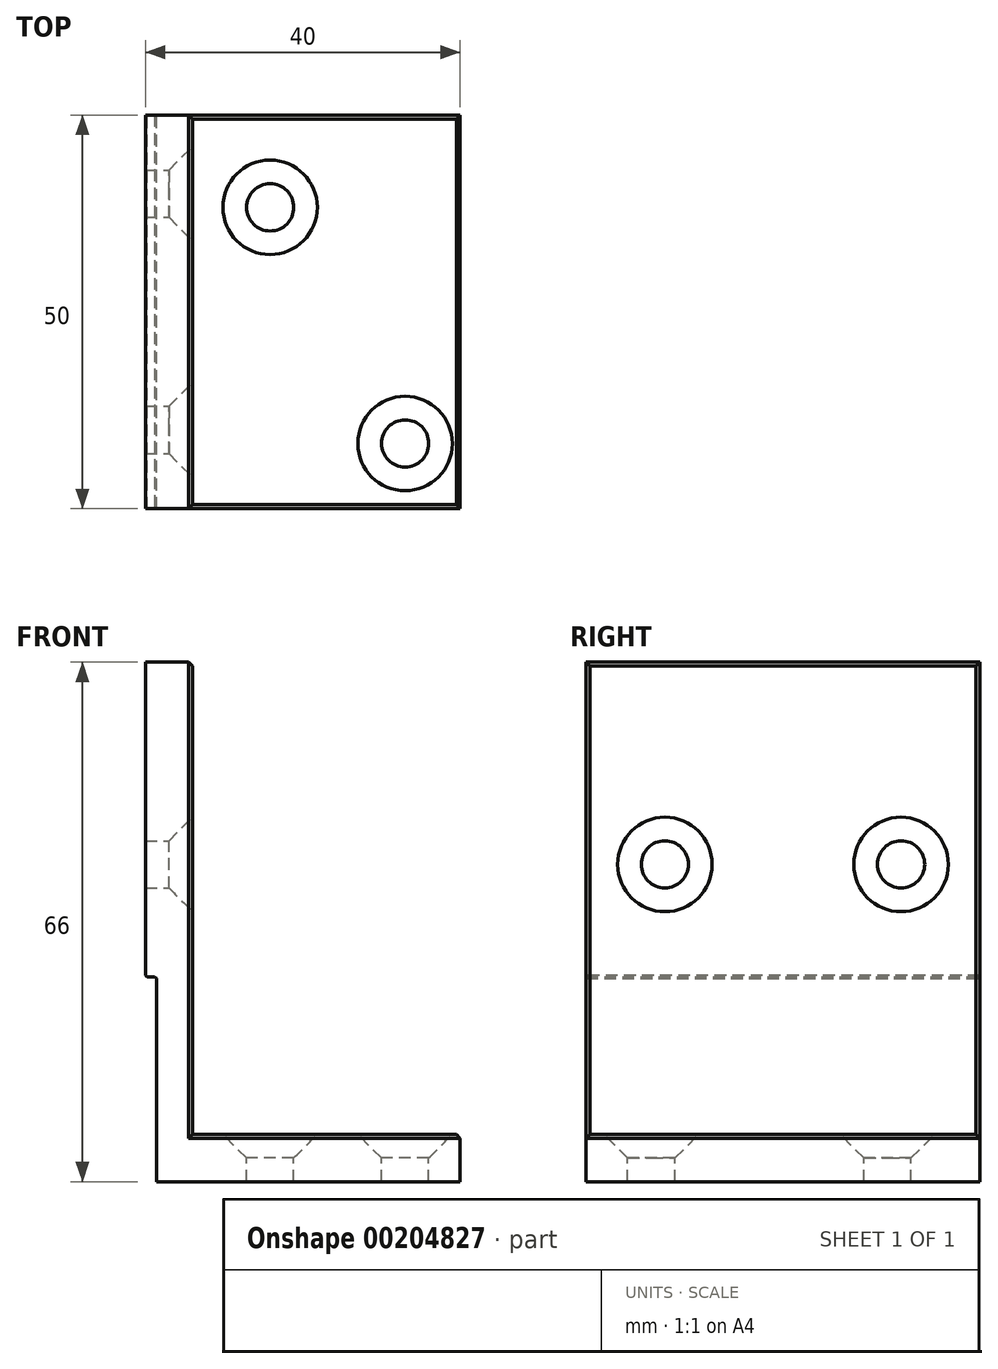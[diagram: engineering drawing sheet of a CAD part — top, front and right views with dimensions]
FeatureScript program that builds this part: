
annotation { "Feature Type Name" : "Feature", "Feature Type Description" : "" }
export const myFeature = defineFeature(function(context is Context, id is Id, definition is map)
    precondition{}
    {
        {
            var Q0;
            Q0=qCreatedBy(makeId("Front.planeOp"),FACE);
            var sketch = newSketch(context, id + "F0", { "sketchPlane" : qUnion([Q0])});
            skLineSegment(sketch, "E0", {"start": v(0, 0) * mm, "end": v(38.6, 0) * mm});
            skLineSegment(sketch, "E1", {"start": v(38.6, 0) * mm, "end": v(38.6, 6) * mm});
            skLineSegment(sketch, "E2", {"start": v(38.6, 6) * mm, "end": v(4.6, 6) * mm});
            skLineSegment(sketch, "E3", {"start": v(4.6, 6) * mm, "end": v(4.6, 66) * mm});
            skLineSegment(sketch, "E4", {"start": v(4.6, 66) * mm, "end": v(-1.4, 66) * mm});
            skLineSegment(sketch, "E5", {"start": v(-1.4, 66) * mm, "end": v(-1.4, 26) * mm});
            skLineSegment(sketch, "E6", {"start": v(-1.4, 26) * mm, "end": v(0, 26) * mm});
            skLineSegment(sketch, "E7", {"start": v(0, 26) * mm, "end": v(0, 0) * mm});
            skSolve(sketch);
        }
        {
            var Q0;
            Q0=makeQuery(id+"F0.imprint","IMPRINT",FACE,{"disambiguationData":[TD([[makeQuery(id+"F0.imprint","IMPRINT",EDGE,{"derivedFrom":sQuery(id+"F0.wireOp",EDGE,"E0")}),1.0]])]});
            extrude(context, id + "F1", {"entities" : qUnion([Q0]), "depth" : 50 * mm});
        }
        {
            var Q0;
            Q0=makeQuery(id+"F1.opExtrude","SWEPT_FACE",FACE,{"disambiguationData":[OSD([sQuery(id+"F0.wireOp",EDGE,"E3")])]});
            var sketch = newSketch(context, id + "F2", { "sketchPlane" : qUnion([Q0])});
            skCircle(sketch, "E8", {"center": v(-40, 40.3) * mm, "radius": 3 * mm});
            skCircle(sketch, "E9", {"center": v(-10, 40.3) * mm, "radius": 3 * mm});
            skSolve(sketch);
        }
        {
            var Q0;
            Q0=sQuery(id+"F2.wireOp",VERTEX,"E8.center");
            var Q1;
            Q1=sQuery(id+"F2.wireOp",VERTEX,"E9.center");
            var Q2;
            Q2=makeQuery(id+"F1.opExtrude","SWEPT_BODY",BODY,{"disambiguationData":[OSD([sQuery(id+"F0.wireOp",EDGE,"E0"),sQuery(id+"F0.wireOp",EDGE,"E1"),sQuery(id+"F0.wireOp",EDGE,"E2"),sQuery(id+"F0.wireOp",EDGE,"E3"),sQuery(id+"F0.wireOp",EDGE,"E4"),sQuery(id+"F0.wireOp",EDGE,"E5"),sQuery(id+"F0.wireOp",EDGE,"E6"),sQuery(id+"F0.wireOp",EDGE,"E7")])]});
            hole(context, id + "F3", {"style" : HoleStyle.C_SINK, "endStyle" : HoleEndStyle.BLIND, "holeDiameter" : 6 * mm, "cSinkDiameter" : 12 * mm, "cSinkAngle" : 90 * degree, "holeDepth" : 12 * mm, "startFromSketch" : true, "locations" : qUnion([Q0, Q1]), "scope" : qUnion([Q2])});
        }
        {
            var Q0;
            Q0=makeQuery(id+"F1.opExtrude","SWEPT_FACE",FACE,{"disambiguationData":[OSD([sQuery(id+"F0.wireOp",EDGE,"E2")])]});
            var sketch = newSketch(context, id + "F4", { "sketchPlane" : qUnion([Q0])});
            skCircle(sketch, "E10", {"center": v(14.45, -11.73) * mm, "radius": 3 * mm});
            skCircle(sketch, "E11", {"center": v(31.6, -41.73) * mm, "radius": 3 * mm});
            skSolve(sketch);
        }
        {
            var Q0;
            Q0=sQuery(id+"F4.wireOp",VERTEX,"E10.center");
            var Q1;
            Q1=sQuery(id+"F4.wireOp",VERTEX,"E11.center");
            var Q2;
            Q2=makeQuery(id+"F1.opExtrude","SWEPT_BODY",BODY,{"disambiguationData":[OSD([sQuery(id+"F0.wireOp",EDGE,"E0"),sQuery(id+"F0.wireOp",EDGE,"E1"),sQuery(id+"F0.wireOp",EDGE,"E2"),sQuery(id+"F0.wireOp",EDGE,"E3"),sQuery(id+"F0.wireOp",EDGE,"E4"),sQuery(id+"F0.wireOp",EDGE,"E5"),sQuery(id+"F0.wireOp",EDGE,"E6"),sQuery(id+"F0.wireOp",EDGE,"E7")])]});
            hole(context, id + "F5", {"style" : HoleStyle.C_SINK, "endStyle" : HoleEndStyle.BLIND, "holeDiameter" : 6 * mm, "cSinkDiameter" : 12 * mm, "cSinkAngle" : 90 * degree, "holeDepth" : 12 * mm, "startFromSketch" : true, "locations" : qUnion([Q0, Q1]), "scope" : qUnion([Q2])});
        }
        {
            var Q0;
            Q0=makeQuery(id+"F1.opExtrude","SWEPT_EDGE",EDGE,{"disambiguationData":[OSD([sQuery(id+"F0.wireOp",EDGE,"E3"),sQuery(id+"F0.wireOp",EDGE,"E4")])]});
            var Q1;
            Q1=makeQuery(id+"F1.opExtrude","CAP_EDGE",EDGE,{"disambiguationData":[OSD([sQuery(id+"F0.wireOp",EDGE,"E3")])],"isStart":false});
            var Q2;
            Q2=makeQuery(id+"F1.opExtrude","CAP_EDGE",EDGE,{"disambiguationData":[OSD([sQuery(id+"F0.wireOp",EDGE,"E3")])],"isStart":true});
            var Q3;
            Q3=makeQuery(id+"F1.opExtrude","CAP_EDGE",EDGE,{"disambiguationData":[OSD([sQuery(id+"F0.wireOp",EDGE,"E2")])],"isStart":false});
            var Q4;
            Q4=makeQuery(id+"F1.opExtrude","SWEPT_EDGE",EDGE,{"disambiguationData":[OSD([sQuery(id+"F0.wireOp",EDGE,"E1"),sQuery(id+"F0.wireOp",EDGE,"E2")])]});
            var Q5;
            Q5=makeQuery(id+"F1.opExtrude","CAP_EDGE",EDGE,{"disambiguationData":[OSD([sQuery(id+"F0.wireOp",EDGE,"E2")])],"isStart":true});
            chamfer(context, id + "F6", {"entities" : qUnion([Q0, Q1, Q2, Q3, Q4, Q5]), "width" : .5 * mm, "tangentPropagation" : true});
        }
        {
            var Q0;
            Q0=makeQuery(id+"F1.opExtrude","SWEPT_EDGE",EDGE,{"disambiguationData":[OSD([sQuery(id+"F0.wireOp",EDGE,"E5"),sQuery(id+"F0.wireOp",EDGE,"E6")])]});
            var Q1;
            Q1=makeQuery(id+"F1.opExtrude","SWEPT_EDGE",EDGE,{"disambiguationData":[OSD([sQuery(id+"F0.wireOp",EDGE,"E6"),sQuery(id+"F0.wireOp",EDGE,"E7")])]});
            chamfer(context, id + "F7", {"entities" : qUnion([Q0, Q1]), "width" : 0.2 * mm, "tangentPropagation" : true});
        }
    });
